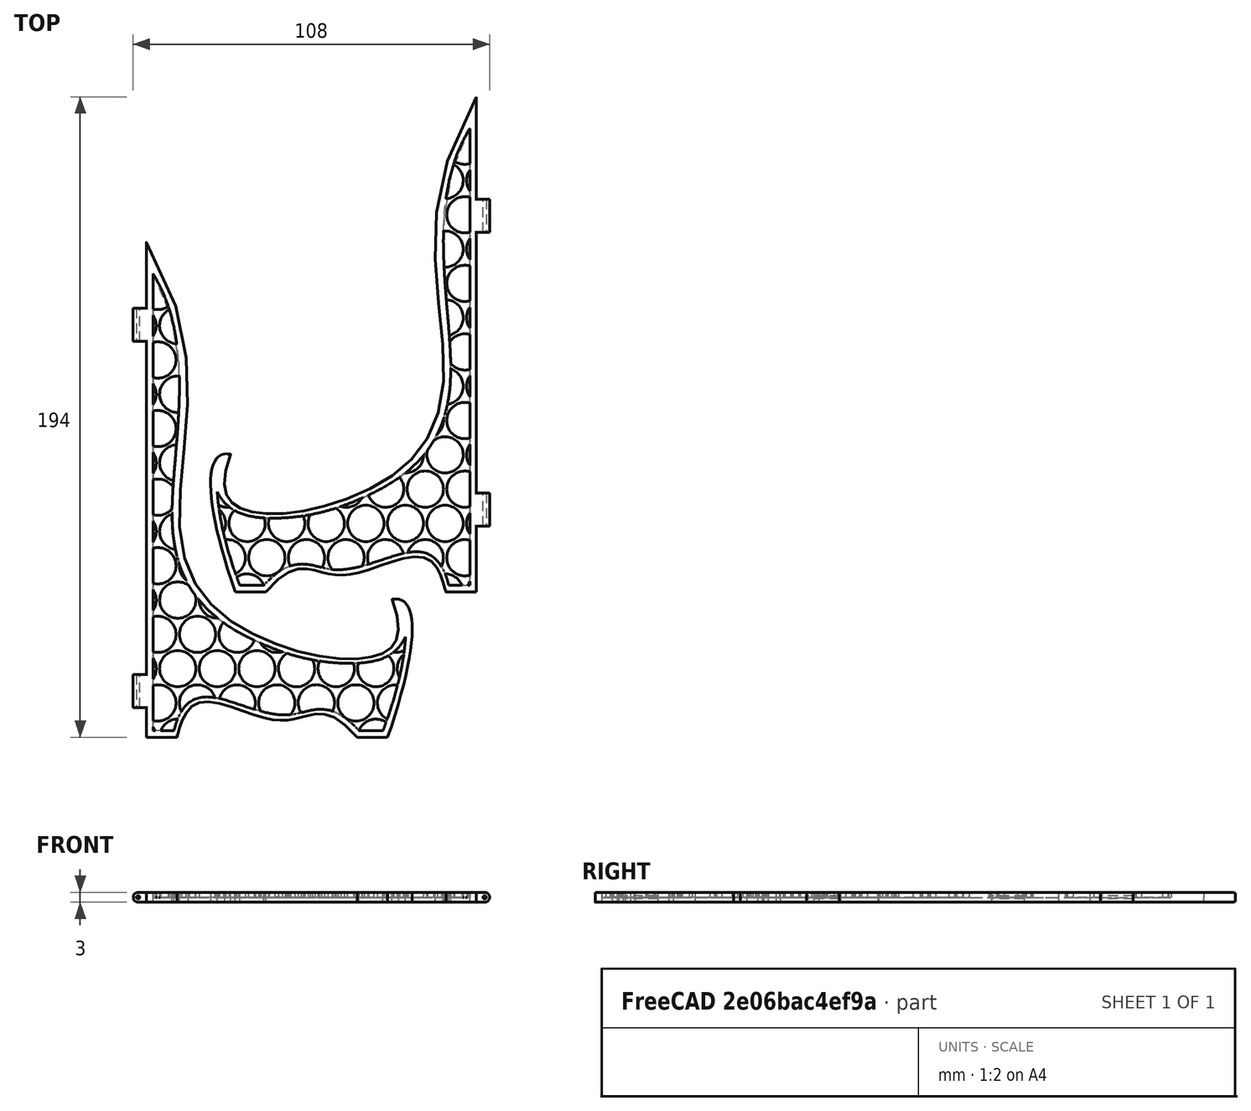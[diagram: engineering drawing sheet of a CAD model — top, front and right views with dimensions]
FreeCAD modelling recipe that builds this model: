
FCSTD DOCUMENT  (FreeCAD 0.20R27319 (Git))
Label: Plate Stand pin hinge V2
License: All rights reserved
LicenseURL: http://en.wikipedia.org/wiki/All_rights_reserved
objects: Sketcher::SketchObject×4, PartDesign::Pad×4, PartDesign::Body×4, Part::MultiFuse×4, Part::Mirroring×3, PartDesign::Fillet×2, Part::FeaturePython×2, Spreadsheet::Sheet×1, Part::Feature×1, Part::MultiCommon×1
note: 31 computed .brp shape members not serialized (recipe doc carries the construction recipe); baked Part::Feature solids carry a one-line shape summary decoded from their .brp

FEATURE [Spreadsheet::Sheet] Spreadsheet
  cells = A1=Height; B1(Height)=150; A2=Depth; B2(Depth)=150; A3=Thickness; B3(Thickness)=3; A4=XScale; B4(XScale)==Depth / 100; A5=YScale; B5(YScale)==Height / 150; A6=ZScale; B6(ZScale)==Thickness / 3; A7=Axle Diameter; B7(AxleDiameter)=1.5; A8=ControlDimension; B8(ControlDimension)=12; A9=X_Repeat; B9(X_Repeat)=8; A10=Y_Repeat; B10(Y_Repeat)=7; A11=Hex Thickness; B11(HexThickness)=1
FEATURE [Sketcher::SketchObject] Sketch  label="Right outline"
  FullyConstrained = false
  MapMode = 5
  Support = -> [XY_Plane]
  expr: Constraints[40] = 150 - 3
  sketch-geometry (36):
    g0-g3: Circle x4 (B-spline internal-alignment scaffolding for g4; pole/knot coordinates omitted)
    g4: BSplineCurve PolesCount=4 KnotsCount=2 Degree=3 IsPeriodic=0
    g5: GeomPoint X=79.7929 Y=34.1576 Z=0
    g6: GeomPoint X=74.5081 Y=0 Z=0
    g7: LineSegment StartX=3.5 StartY=0 StartZ=0 EndX=10.7553 EndY=0 EndZ=0
    g8: LineSegment StartX=74.5081 StartY=0 StartZ=0 EndX=67.4708 EndY=0 EndZ=0
    g9-g15: Circle x7 (B-spline internal-alignment scaffolding for g16; pole/knot coordinates omitted)
    g16: BSplineCurve PolesCount=7 KnotsCount=5 Degree=3 IsPeriodic=0
    g17-g21: GeomPoint x5 (B-spline internal-alignment scaffolding for g16; pole/knot coordinates omitted)
    g22: LineSegment StartX=3.5 StartY=147 StartZ=0 EndX=3.5 EndY=0 EndZ=0
    g23-g29: Circle x7 (B-spline internal-alignment scaffolding for g30; pole/knot coordinates omitted)
    g30: BSplineCurve PolesCount=7 KnotsCount=5 Degree=3 IsPeriodic=0
    g31-g35: GeomPoint x5 (B-spline internal-alignment scaffolding for g30; pole/knot coordinates omitted)
  constraints (30):
    c: PointOnObject(g4,g-1)
    c: Weight(g0) = 1
    c: Equal(g0,g1)
    c: Equal(g0,g2)
    c: Equal(g0,g3)
    c: InternalAlignment(g0-g3 -> g4) x4
    c: InternalAlignment(g5,g4)
    c: InternalAlignment(g6,g4)
    c: PointOnObject(g7,g-1)
    c: Coincident(g8,g4)
    c: PointOnObject(g8,g-1)
    c: Coincident(g16,g7)
    c: Weight(g9) = 1
    c: Equal(g9,g10)
    c: PointOnObject(g10,g9)
    c: Equal(g9, g11-g15) x5
    c: Coincident(g16,g8)
    c: InternalAlignment(g9-g15 -> g16) x7
    c: InternalAlignment(g17-g21 -> g16) x5
    c: Coincident(g22,g7)
    c: Horizontal(g7)
    c: DistanceX(g-1,g7) = 3.5
    c: Vertical(g22)
    c: DistanceY(g7,g22) = 147
    c: Weight(g23) = 1
    c: Equal(g23, g26-g29) x4
    c: Coincident(g30,g4)
    c: InternalAlignment(g23-g29 -> g30) x7
    c: InternalAlignment(g31-g35 -> g30) x5
    c: Coincident(g30,g22)
FEATURE [PartDesign::Pad] Pad  label="Right"
  Direction = (0,0,1)
  Length = 3
  Length2 = 10
  Midplane = true
  Profile = -> Sketch
  ReferenceAxis = -> Sketch [N_Axis]
  Type = 0
FEATURE [PartDesign::Body] Body  label="Right Body Solid"
  Group = -> [Sketch,Pad]
  Origin = -> Origin
  Tip = -> Pad
FEATURE [Sketcher::SketchObject] Sketch001
  FullyConstrained = true
  MapMode = 5
  Placement = pos=(0,0,0) rot=(1,0,0;1.5708rad)
  Support = -> [XZ_Plane001]
  sketch-geometry (5):
    g0: LineSegment StartX=-2e-16 StartY=1.5 StartZ=0 EndX=4 EndY=1.5 EndZ=0
    g1: LineSegment StartX=4 StartY=1.5 StartZ=0 EndX=4 EndY=-1.5 EndZ=0
    g2: LineSegment StartX=4 StartY=-1.5 StartZ=0 EndX=-4e-16 EndY=-1.5 EndZ=0
    g3: ArcOfCircle CenterX=0 CenterY=0 CenterZ=0 NormalX=0 NormalY=0 NormalZ=1 AngleXU=0 Radius=1.5 StartAngle=1.5708 EndAngle=4.71239
    g4: Circle CenterX=0 CenterY=0 CenterZ=0 NormalX=0 NormalY=0 NormalZ=1 AngleXU=0 Radius=0.5
  constraints (13):
    c: PointOnObject(g0,g-2)
    c: Horizontal(g0)
    c: Coincident(g0,g1)
    c: Vertical(g1)
    c: Coincident(g1,g2)
    c: PointOnObject(g2,g-2)
    c: Tangent(g2,g3) = 1.5708
    c: Coincident(g3,g0)
    c: Coincident(g3,g-1)
    c: Coincident(g4,g3)
    c: Diameter(g3) = 3
    c: Distance(g0) = 4
    c: Diameter(g4) = 1
FEATURE [PartDesign::Pad] Pad001
  Direction = (0,-1,-2e-16)
  Length = 10
  Length2 = 10
  Placement = pos=(0,0,0) rot=(1,0,0;1.5708rad)
  Profile = -> Sketch001
  ReferenceAxis = -> Sketch001 [N_Axis]
  Reversed = true
  Type = 0
FEATURE [PartDesign::Body] Body001  label="Hinge Half Right Lower"
  Group = -> [Sketch001,Pad001]
  Origin = -> Origin001
  Placement = pos=(0,9,0) rot=(0,0,1;0rad)
  Tip = -> Pad001
FEATURE [Part::Feature] Body001001  label="Hinge Half Right Upper"
  Placement = pos=(0,120,0) rot=(0,0,1;0rad)
  shape: bbox 5.5 x 10 x 3 mm, 7 faces (baked)
FEATURE [Sketcher::SketchObject] Sketch004  label="Right Body Edge Sketch"
  FullyConstrained = false
  MapMode = 5
  Support = -> [XY_Plane004]
  sketch-geometry (69):
    g0-g3: Circle x4 (B-spline internal-alignment scaffolding for g4; pole/knot coordinates omitted)
    g4: BSplineCurve PolesCount=4 KnotsCount=2 Degree=3 IsPeriodic=0
    g5: GeomPoint X=76.9837 Y=41.8126 Z=0
    g6: GeomPoint X=75.5652 Y=0 Z=0
    g7: LineSegment StartX=2.5 StartY=0 StartZ=0 EndX=11.7172 EndY=0 EndZ=0
    g8: LineSegment StartX=75.5652 StartY=0 StartZ=0 EndX=66.348 EndY=0 EndZ=0
    g9-g15: Circle x7 (B-spline internal-alignment scaffolding for g16; pole/knot coordinates omitted)
    g16: BSplineCurve PolesCount=7 KnotsCount=5 Degree=3 IsPeriodic=0
    g17-g21: GeomPoint x5 (B-spline internal-alignment scaffolding for g16; pole/knot coordinates omitted)
    g22: LineSegment StartX=2.5 StartY=150 StartZ=0 EndX=2.5 EndY=0 EndZ=0
    g23-g29: Circle x7 (B-spline internal-alignment scaffolding for g30; pole/knot coordinates omitted)
    g30: BSplineCurve PolesCount=7 KnotsCount=5 Degree=3 IsPeriodic=0
    g31-g35: GeomPoint x5 (B-spline internal-alignment scaffolding for g30; pole/knot coordinates omitted)
    g36: LineSegment StartX=4.5 StartY=2 StartZ=0 EndX=10.8659 EndY=2 EndZ=0
    g37-g43: Circle x7 (B-spline internal-alignment scaffolding for g44; pole/knot coordinates omitted)
    g44: BSplineCurve PolesCount=7 KnotsCount=5 Degree=3 IsPeriodic=0
    g45-g48: GeomPoint x4 (B-spline internal-alignment scaffolding for g44; pole/knot coordinates omitted)
    g49-g52: Circle x4 (B-spline internal-alignment scaffolding for g53; pole/knot coordinates omitted)
    g53: BSplineCurve PolesCount=4 KnotsCount=2 Degree=3 IsPeriodic=0
    g54: GeomPoint X=81.0103 Y=30.4239 Z=0
    g55: GeomPoint X=74.1946 Y=2 Z=0
    g56: LineSegment StartX=74.1946 StartY=2 StartZ=0 EndX=66.9285 EndY=2 EndZ=0
    g57: LineSegment StartX=4.5 StartY=140.48 StartZ=0 EndX=4.5 EndY=2 EndZ=0
    g58-g63: Circle x6 (B-spline internal-alignment scaffolding for g64; pole/knot coordinates omitted)
    g64: BSplineCurve PolesCount=6 KnotsCount=4 Degree=3 IsPeriodic=0
    g65-g68: GeomPoint x4 (B-spline internal-alignment scaffolding for g64; pole/knot coordinates omitted)
  constraints (62):
    c: Weight(g0) = 1
    c: Equal(g0,g1)
    c: Equal(g0,g2)
    c: Equal(g0,g3)
    c: InternalAlignment(g0-g3 -> g4) x4
    c: InternalAlignment(g5,g4)
    c: InternalAlignment(g6,g4)
    c: PointOnObject(g7,g-1)
    c: PointOnObject(g8,g-1)
    c: Equal(g7,g8)
    c: Coincident(g16,g7)
    c: Weight(g9) = 1
    c: Equal(g9,g10)
    c: PointOnObject(g10,g9)
    c: Equal(g9, g11-g15) x5
    c: Coincident(g16,g8)
    c: InternalAlignment(g9-g15 -> g16) x7
    c: InternalAlignment(g17-g21 -> g16) x5
    c: Coincident(g22,g7)
    c: Horizontal(g7)
    c: DistanceX(g-1,g7) = 2.5
    c: Vertical(g22)
    c: DistanceY(g7,g22) = 150
    c: Weight(g23) = 1
    c: Equal(g23, g26-g29) x4
    c: Coincident(g30,g4)
    c: InternalAlignment(g23-g29 -> g30) x7
    c: InternalAlignment(g31-g35 -> g30) x5
    c: Horizontal(g36)
    c: Weight(g37) = 1
    c: Equal(g37, g38-g43) x6
    c: InternalAlignment(g37-g43 -> g44) x7
    c: InternalAlignment(g45-g48 -> g44) x4
    c: Coincident(g53,g44)
    c: Weight(g49) = 1
    c: Equal(g49,g50)
    c: Equal(g49,g51)
    c: Equal(g49,g52)
    c: InternalAlignment(g49-g52 -> g53) x4
    c: InternalAlignment(g54,g53)
    c: InternalAlignment(g55,g53)
    c: Coincident(g56,g53)
    c: Horizontal(g56)
    c: Coincident(g57,g37)
    c: Coincident(g57,g36)
    c: Vertical(g57)
    c: Horizontal(g36,g56)
    c: DistanceX(g7,g36) = 2
    c: Block(g30)
    c: PointOnObject(g8,g-1)
    c: Coincident(g8,g4)
    c: DistanceY(g4,g53) = 2
    c: Block(g7)
    c: Block(g8)
    c: Block(g16)
    c: Coincident(g64,g36)
    c: Weight(g58) = 1
    c: Equal(g58, g59-g63) x5
    c: Coincident(g64,g56)
    c: InternalAlignment(g58-g63 -> g64) x6
    c: InternalAlignment(g65-g68 -> g64) x4
    c: Block(g56)
FEATURE [PartDesign::Pad] Pad004  label="Right Edge"
  Direction = (0,0,1)
  Length = 3
  Length2 = 10
  Midplane = true
  Profile = -> Sketch004
  ReferenceAxis = -> Sketch004 [N_Axis]
  Type = 0
FEATURE [Sketcher::SketchObject] Sketch005
  FullyConstrained = true
  MapMode = 5
  Support = -> [XY_Plane005]
  expr: Constraints[21] = Spreadsheet.ControlDimension
  expr: Constraints[28] = Spreadsheet.HexThickness / 2
  sketch-geometry (10):
    g0: LineSegment StartX=6 StartY=-3.4641 StartZ=0 EndX=6 EndY=3.4641 EndZ=0
    g1: LineSegment StartX=6 StartY=3.4641 StartZ=0 EndX=-9e-16 EndY=6.9282 EndZ=0
    g2: LineSegment StartX=-9e-16 StartY=6.9282 StartZ=0 EndX=-6 EndY=3.4641 EndZ=0
    g3: LineSegment StartX=-6 StartY=3.4641 StartZ=0 EndX=-6 EndY=-3.4641 EndZ=0
    g4: LineSegment StartX=-6 StartY=-3.4641 StartZ=0 EndX=9e-16 EndY=-6.9282 EndZ=0
    g5: LineSegment StartX=9e-16 StartY=-6.9282 StartZ=0 EndX=6 EndY=-3.4641 EndZ=0
    g6: Circle CenterX=0 CenterY=0 CenterZ=0 NormalX=0 NormalY=0 NormalZ=1 AngleXU=0 Radius=6.9282
    g7: Circle CenterX=0 CenterY=0 CenterZ=0 NormalX=0 NormalY=0 NormalZ=1 AngleXU=0 Radius=5.5
    g8: LineSegment StartX=0 StartY=0 StartZ=0 EndX=3 EndY=-5.19615 EndZ=0
    g9: GeomPoint X=2.75 Y=-4.76314 Z=0
  constraints (25):
    c: Coincident(g0,g1)
    c: Coincident(g1,g2)
    c: Coincident(g2,g3)
    c: Coincident(g3,g4)
    c: Coincident(g4,g5)
    c: Coincident(g5,g0)
    c: Equal(g0, g1-g5) x5
    c: PointOnObject(g0,g6)
    c: PointOnObject(g1,g6)
    c: PointOnObject(g2,g6)
    c: PointOnObject(g3,g6)
    c: PointOnObject(g4,g6)
    c: PointOnObject(g5,g6)
    c: Coincident(g6,g-1)
    c: Vertical(g0)
    c: DistanceY(g0,g1) = 10.3923
    c: DistanceY(g3,g3) = 6.9282
    c: DistanceX(g2,g0) = 12
    c: Coincident(g7,g6)
    c: Coincident(g8,g7)
    c: Perpendicular(g8,g5)
    c: PointOnObject(g8,g5)
    c: PointOnObject(g9,g8)
    c: PointOnObject(g9,g7)
    c: Distance(g9,g8) = 0.5
FEATURE [PartDesign::Pad] Pad005  label="Hex Basic"
  Direction = (0,0,1)
  Length = 3
  Length2 = 10
  Profile = -> Sketch005
  ReferenceAxis = -> Sketch005 [N_Axis]
  Type = 0
  expr: Length = Spreadsheet.Thickness
FEATURE [PartDesign::Fillet] Fillet
  Base = -> Pad005 [Edge21,Edge20]
  BaseFeature = -> Pad005
  Radius = 0.2
  SupportTransform = false
FEATURE [PartDesign::Body] Body001001005  label="Hex"
  Group = -> [Sketch005,Pad005,Fillet]
  Origin = -> Origin005
  Tip = -> Fillet
FEATURE [Part::FeaturePython] Clone  label="Hex Offset"  # Draft clone (typed FeaturePython)
  AttacherType = Attacher::AttachEngine3D
  Fuse = false
  Objects = -> [Body001001005]
  Placement = pos=(6,10.3923,0) rot=(0,0,1;0rad)
  Scale = (1,1,1)
  expr: .Placement.Base.x = Spreadsheet.ControlDimension / 2
  expr: .Placement.Base.y = Spreadsheet.ControlDimension * sin(60)
FEATURE [Part::MultiFuse] Fusion  label="Hex Pair"
  Shapes = -> [Body001001005,Clone]
FEATURE [Part::FeaturePython] Array002  label="Hex array"  # Draft array (typed FeaturePython)
  AlwaysSyncPlacement = false
  Angle = 360
  ArrayType = 0
  Axis = (0,0,1)
  Base = -> Fusion
  Center = (0,0,0)
  Count = 56
  ExpandArray = false
  Fuse = true
  IntervalAxis = (0,0,0)
  IntervalX = (12,0,0)
  IntervalY = (0,20.7846,0)
  IntervalZ = (0,0,100)
  NumberCircles = 3
  NumberPolar = 5
  NumberX = 8
  NumberY = 7
  NumberZ = 1
  PlacementList = 56 placements: [(0,0,0),(0,20.7846,0),(0,41.5692,0),(0,62.3538,0),(0,83.1384,0),(0,103.923,0),(0,124.708,0),(12,0,0),(12,20.7846,0),(12,41.5692,0),(12,62.3538,0),(12,83.1384,0),(12,103.923,0),(12,124.708,0),(24,0,0),(24,20.7846,0),(24,41.5692,0),(24,62.3538,0),(24,83.1384,0),(24,103.923,0),(24,124.708,0),(36,0,0),(36,20.7846,0),(36,41.5692,0),(36,62.3538,0),(36,83.1384,0),(36,103.923,0),(36,124.708,0),(48,0,0),+27 more]
  RadialDistance = 50
  ScaleList = (56) [(1,1,1),(1,1,1),(1,1,1),(1,1,1),(1,1,1),(1,1,1),(1,1,1),(1,1,1),(1,1,1),(1,1,1),(1,1,1),(1,1,1),(1,1,1),(1,1,1),(1,1,1),(1,1,1),(1,1,1),(1,1,1),+38 more]
  Symmetry = 1
  TangentialDistance = 25
  expr: .IntervalX.x = Spreadsheet.ControlDimension
  expr: .IntervalY.y = 2 * Spreadsheet.ControlDimension * sin(60)
  expr: NumberX = Spreadsheet.X_Repeat
  expr: NumberY = Spreadsheet.Y_Repeat
FEATURE [Part::MultiCommon] Common  label="Right Hex interior"
  Refine = true
  Shapes = -> [Array002,Body]
FEATURE [Part::Mirroring] Part__Mirroring001  label="Hinge Half Right Lower (Mirror #2)"
  Base = (0,0,0)
  Normal = (1,0,0)
  Placement = pos=(0,11,0) rot=(0,0,1;0rad)
  Source = -> Body001
FEATURE [Part::Mirroring] Part__Mirroring002  label="Hinge Half Right Upper (Mirror #3)"
  Base = (0,0,0)
  Normal = (1,0,0)
  Placement = pos=(0,-11,0) rot=(0,0,1;0rad)
  Source = -> Body001001
FEATURE [PartDesign::Fillet] Fillet001
  Base = -> Pad004 [Edge3,Edge17,Edge12,Edge6,Edge18,Edge13,Edge4,Edge7]
  BaseFeature = -> Pad004
  Radius = 0.4
  SupportTransform = false
FEATURE [PartDesign::Body] Body001001004  label="Right Edge Body"
  Group = -> [Sketch004,Pad004,Fillet001]
  Origin = -> Origin004
  Tip = -> Fillet001
FEATURE [Part::MultiFuse] Fusion001  label="Right Body"
  Shapes = -> [Body001001004,Common]
FEATURE [Part::MultiFuse] Fusion002  label="Right Complete"
  Placement = pos=(3,0,0) rot=(0,0,1;0rad)
  Shapes = -> [Body001,Body001001,Fusion001]
FEATURE [Part::Mirroring] Part__Mirroring  label="Left Body"
  Base = (0,0,0)
  Normal = (1,0,0)
  Source = -> Fusion001
FEATURE [Part::MultiFuse] Fusion003  label="Left Complete"
  Placement = pos=(108,44,0) rot=(0,0,1;0rad)
  Shapes = -> [Part__Mirroring,Part__Mirroring001,Part__Mirroring002]
